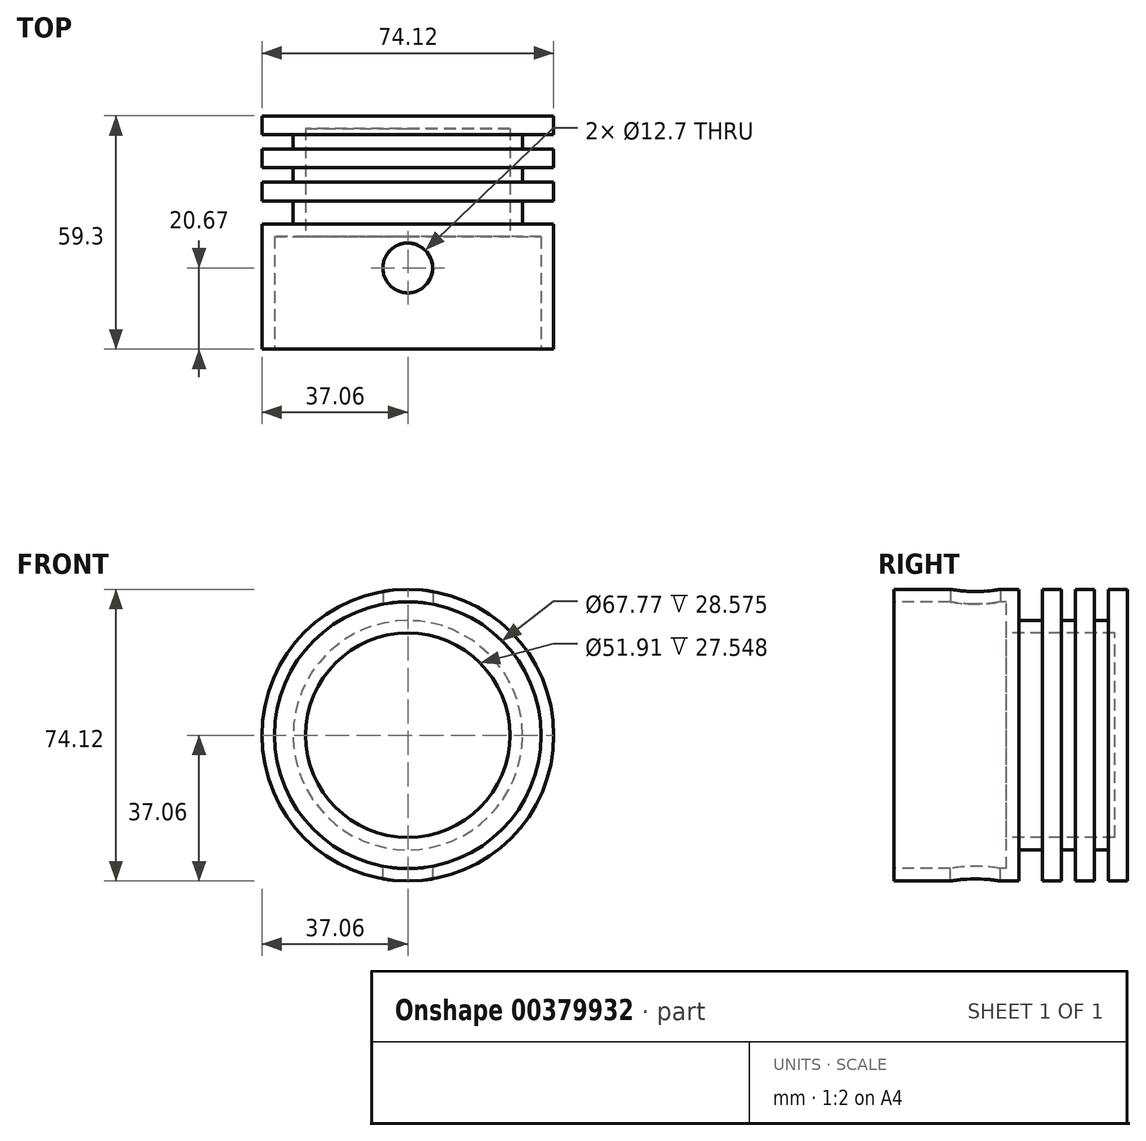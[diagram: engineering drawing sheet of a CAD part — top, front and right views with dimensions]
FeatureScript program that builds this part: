
annotation { "Feature Type Name" : "Feature", "Feature Type Description" : "" }
export const myFeature = defineFeature(function(context is Context, id is Id, definition is map)
    precondition{}
    {
        {
            var Q0;
            Q0=qCreatedBy(makeId("Top.planeOp"),FACE);
            var sketch = newSketch(context, id + "F0", { "sketchPlane" : qUnion([Q0])});
            skLineSegment(sketch, "E0", {"start": v(0, 0) * mm, "end": v(0, 59.3) * mm});
            skLineSegment(sketch, "E1", {"start": v(0, 59.3) * mm, "end": v(-37.06, 59.3) * mm});
            skLineSegment(sketch, "E2", {"start": v(0, 0) * mm, "end": v(-37.06, 0) * mm});
            skLineSegment(sketch, "E3", {"start": v(-37.06, 59.3) * mm, "end": v(-37.06, 54.5) * mm});
            skLineSegment(sketch, "E4", {"start": v(-37.06, 54.5) * mm, "end": v(-29.13, 54.5) * mm});
            skLineSegment(sketch, "E5", {"start": v(-29.13, 54.5) * mm, "end": v(-29.13, 50.9) * mm});
            skLineSegment(sketch, "E6", {"start": v(-29.13, 50.9) * mm, "end": v(-37.06, 50.9) * mm});
            skLineSegment(sketch, "E7", {"start": v(-37.06, 50.9) * mm, "end": v(-37.06, 46.1) * mm});
            skLineSegment(sketch, "E8", {"start": v(-37.06, 46.1) * mm, "end": v(-29.13, 46.1) * mm});
            skLineSegment(sketch, "E9", {"start": v(-29.13, 46.1) * mm, "end": v(-29.13, 42.48) * mm});
            skLineSegment(sketch, "E10", {"start": v(-29.13, 42.48) * mm, "end": v(-37.06, 42.48) * mm});
            skLineSegment(sketch, "E11", {"start": v(-37.06, 42.48) * mm, "end": v(-37.06, 37.68) * mm});
            skLineSegment(sketch, "E12", {"start": v(-37.06, 37.68) * mm, "end": v(-29.13, 37.68) * mm});
            skLineSegment(sketch, "E13", {"start": v(-29.13, 37.68) * mm, "end": v(-29.13, 31.75) * mm});
            skLineSegment(sketch, "E14", {"start": v(-29.13, 31.75) * mm, "end": v(-37.06, 31.75) * mm});
            skLineSegment(sketch, "E15", {"start": v(-37.06, 31.75) * mm, "end": v(-37.06, 0) * mm});
            skSolve(sketch);
        }
        {
            var Q0;
            Q0=makeQuery(id+"F0.imprint","IMPRINT",FACE,{"disambiguationData":[TD([[makeQuery(id+"F0.imprint","IMPRINT",EDGE,{"derivedFrom":sQuery(id+"F0.wireOp",EDGE,"E0")}),1.0]])]});
            var Q1;
            Q1=sQuery(id+"F0.wireOp",EDGE,"E0");
            revolve(context, id + "F1", {"entities" : qUnion([Q0]), "axis" : qUnion([Q1]), "revolveType" : RevolveType.FULL});
        }
        {
            var Q0;
            Q0=makeQuery(id+"F1.opRevolve","SWEPT_FACE",FACE,{"disambiguationData":[OSD([sQuery(id+"F0.wireOp",EDGE,"E2")])]});
            shell(context, id + "F2", {"entities" : qUnion([Q0]), "thickness" : 3.17 * mm});
        }
        {
            var Q0;
            Q0=qCreatedBy(makeId("Top.planeOp"),FACE);
            var sketch = newSketch(context, id + "F3", { "sketchPlane" : qUnion([Q0])});
            skCircle(sketch, "E16", {"center": v(0, 20.67) * mm, "radius": 6.35 * mm});
            skSolve(sketch);
        }
        {
            var Q0;
            Q0 = qSketchRegion(id + "F3", true);
            extrude(context, id + "F4", {"entities" : qUnion([Q0]), "operationType" : NewBodyOperationType.REMOVE, "oppositeDirection" : true, "depth" : 64 * mm});
        }
        {
            var Q0;
            Q0 = qSketchRegion(id + "F3", true);
            extrude(context, id + "F5", {"entities" : qUnion([Q0]), "operationType" : NewBodyOperationType.REMOVE, "depth" : 104.14 * mm});
        }
    });
